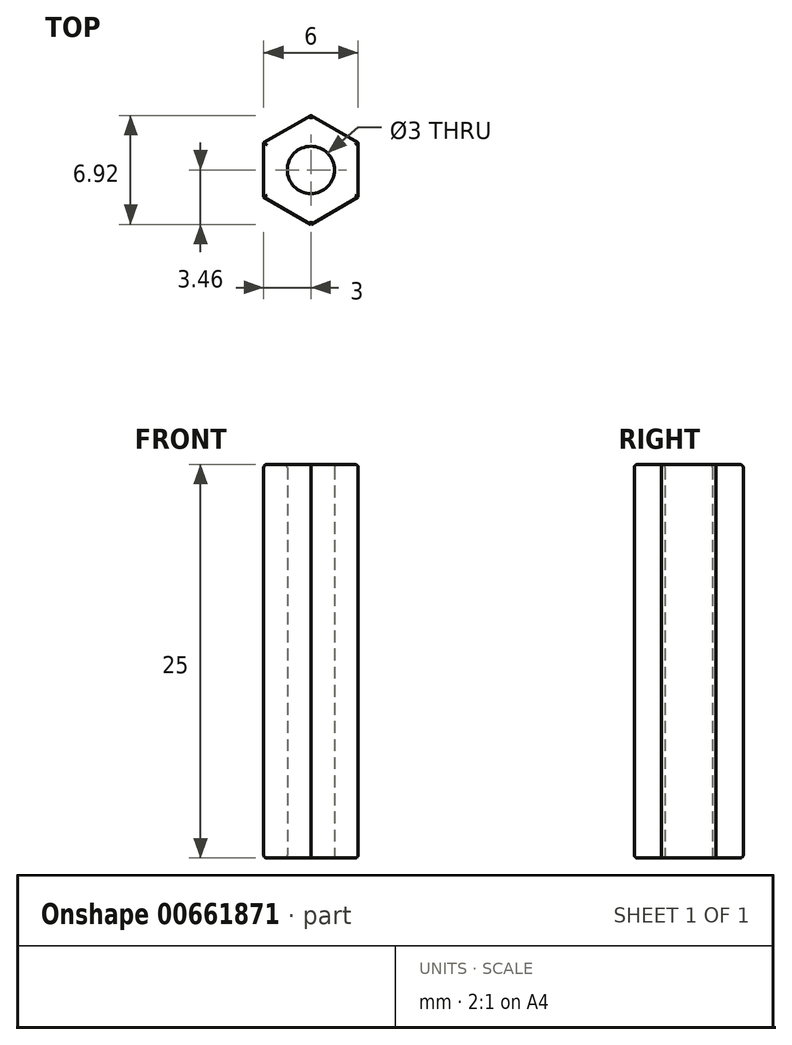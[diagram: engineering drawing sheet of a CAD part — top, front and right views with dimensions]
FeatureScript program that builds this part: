
annotation { "Feature Type Name" : "Feature", "Feature Type Description" : "" }
export const myFeature = defineFeature(function(context is Context, id is Id, definition is map)
    precondition{}
    {
        {
            var Q0;
            Q0=qCreatedBy(makeId("Top.planeOp"),FACE);
            var sketch = newSketch(context, id + "F0", { "sketchPlane" : qUnion([Q0])});
            skCircle(sketch, "E0.cCircle", {"center": v(0, 0) * mm, "radius": 3 * mm, "construction": true});
            skLineSegment(sketch, "E0.0", {"start": v(0, 3.46) * mm, "end": v(3, 1.73) * mm});
            skLineSegment(sketch, "E0.1", {"start": v(3, 1.73) * mm, "end": v(3, -1.73) * mm});
            skLineSegment(sketch, "E0.2", {"start": v(3, -1.73) * mm, "end": v(0, -3.46) * mm});
            skLineSegment(sketch, "E0.3", {"start": v(0, -3.46) * mm, "end": v(-3, -1.73) * mm});
            skLineSegment(sketch, "E0.4", {"start": v(-3, -1.73) * mm, "end": v(-3, 1.73) * mm});
            skLineSegment(sketch, "E0.5", {"start": v(-3, 1.73) * mm, "end": v(0, 3.46) * mm});
            skPoint(sketch, "E0.0.midPoint", {"position": v(1.5, 2.6) * mm});
            skLineSegment(sketch, "E1", {"start": v(3, 1.73) * mm, "end": v(-3, -1.73) * mm, "construction": true});
            skCircle(sketch, "E2", {"center": v(0, 0) * mm, "radius": 1.5 * mm});
            skSolve(sketch);
        }
        {
            var Q0;
            Q0 = qSketchRegion(id + "F0", true);
            extrude(context, id + "F1", {"entities" : qUnion([Q0]), "depth" : 25 * mm, "offsetDistance" : 25 * mm});
        }
        {
            var Q0;
            Q0=makeQuery(id+"F1.opExtrude","CAP_FACE",FACE,{"disambiguationData":[OSD([sQuery(id+"F0.wireOp",EDGE,"E0.0"),sQuery(id+"F0.wireOp",EDGE,"E0.1"),sQuery(id+"F0.wireOp",EDGE,"E0.2"),sQuery(id+"F0.wireOp",EDGE,"E0.3"),sQuery(id+"F0.wireOp",EDGE,"E0.4"),sQuery(id+"F0.wireOp",EDGE,"E0.5"),sQuery(id+"F0.wireOp",EDGE,"E2")])],"isStart":false});
            var Q1;
            Q1=makeQuery(id+"F1.opExtrude","CAP_FACE",FACE,{"disambiguationData":[OSD([sQuery(id+"F0.wireOp",EDGE,"E0.0"),sQuery(id+"F0.wireOp",EDGE,"E0.1"),sQuery(id+"F0.wireOp",EDGE,"E0.2"),sQuery(id+"F0.wireOp",EDGE,"E0.3"),sQuery(id+"F0.wireOp",EDGE,"E0.4"),sQuery(id+"F0.wireOp",EDGE,"E0.5"),sQuery(id+"F0.wireOp",EDGE,"E2")])],"isStart":true});
            fillet(context, id + "F2", {"entities" : qUnion([Q0, Q1]), "radius" : 0.2 * mm, "tangentPropagation" : true, "allowEdgeOverflow" : false});
        }
    });
